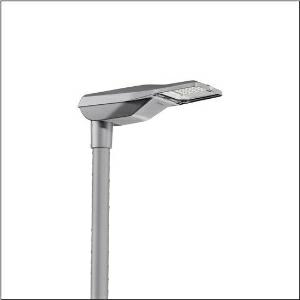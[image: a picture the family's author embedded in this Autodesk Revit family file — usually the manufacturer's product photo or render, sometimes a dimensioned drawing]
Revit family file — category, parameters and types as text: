
# Revit family: streetlight_sl_21_iq_micro___st1_0ab_5xe1m31d08db_7599
name_source: partatom
category: Lighting Fixtures
units: mm (PartAtom-declared; Revit-internal decimal feet)

## family parameters
Cut with Voids When Loaded = No
Host = Face
Light Source = No
Part Type = Normal
Room Calculation Point = No
Round Connector Dimension = Use Diameter
Shared = No

## types (1)
- --- (1 x LED, 4240 lm, 36.4 W, 3000K)
    Apparent Load = 36 VA
    CIE Flux Codes = 38 73 97 100 100
    Color Rendering = 70
    Color Temperature = 3000K
    Default Elevation = 1800 mm
    Description = Streetlight SL 21 iQ micro, mast luminaire, primary light control with lens, of PMMA, primary optical cover: cover, of toughened safety glass, transparent, light distribution: ST1.0aB, light emission: direct distribution, primary light characteristic: asymmetric, installation type: post-top, side-entry, LED, High Power LED, rated luminous flux: 4.240lm, luminous efficacy: 117lm/W, light colour: 730, colour temperature: 3000K, control gear: iQ-Comfort, control: Auto-Match, Temp-Guard, Lumen-Switch, Night-Set, Smart-Wire, Light-Fading, Desk-Remote (wireless, voltage-free reading and setting of iQ features in the workshop via application-optimized NFC function/RFID function), optimised constant luminous flux control (CLO 2.0), pre-setting: linear dimming characteristic, mains connection: 220..240V, AC, 50/60Hz, start of lifetime: 36W, end of service life: 38W, reduction: 16W, luminaire housing, of diecast aluminium, powder-coated, Siteco® metallic grey (DB 702S), corrosivity category C5 mid according to DIN EN ISO 12944, please order mast flange separately, inclination adjustable: 0°, 5°, 10°, 15°, sealing non-destructively replaceable, multi-level sealing system, length: 528mm, width: 235mm, height: 110mm, mast flange for spigot size: 42mm (side-entry): 5XC10008XM4, 60/48mm (side-entry/post-top): 5XC10108XM2, 76/60mm (side-entry/post-top): 5XC10108XM1, protection rating (complete): IP66, insulation class (complete): insulation class II (safety insulation), certification: CE, ENEC, ENEC+, VDE, impact resistance: IK10, permissible operating ambient temperature for outdoor applications: -40..+50°C, standard-compliant lighting for roads and squares, packaging unit: 1 piece

Light Distribution: ST1.0aB
    Height = 110 mm
    Lamp = 1 x LED
    Lamp Light Flux = 4240 lm
    Lamp Power = 36.4 W
    Lamp count = 1
    Length = 528 mm
    Luminous efficacy = 116 lm/W
    Manufacturer = Siteco
    ModVariant = No
    Model = 5XE1M31D08DB
    Number of Poles = 1
    OnlyDefault = Yes
    Power Factor = 1
    Product Name = Streetlight SL 21 iQ micro | ST1.0aB
    Product group = mast luminaire | pylon top
    ProductGroupID = 6100
    Protection Class = Protection class II
    Protection Degree = IP 66
    RLX_Detail_Level = 1
    RLX_Emergency_Light_Flux = 0 lm
    RLX_Emergency_Type = 0
    RLX_Emergency_Type_DB = No
    RlxData = <blob elided: 98829 chars, md5=106855a7>
    Socket = socket
    Standby Power = 0 W
    System Light Flux = 4240 lm
    System Power = 36 W
    Type Comments = factory setting: luminous flux: 100 % | dim-lin: 254 | 715 mA
    Type Image = l_1006881.jpg
    URL = http://relux.com
    VarID = @adj_175571
    Voltage = 0 V
    Weight = 0.00 kg
    Width = 235 mm

## geometry (parser evidence)
native form markers: Blend x4, Sweep x10
no freeform markers — native parametric forms only
